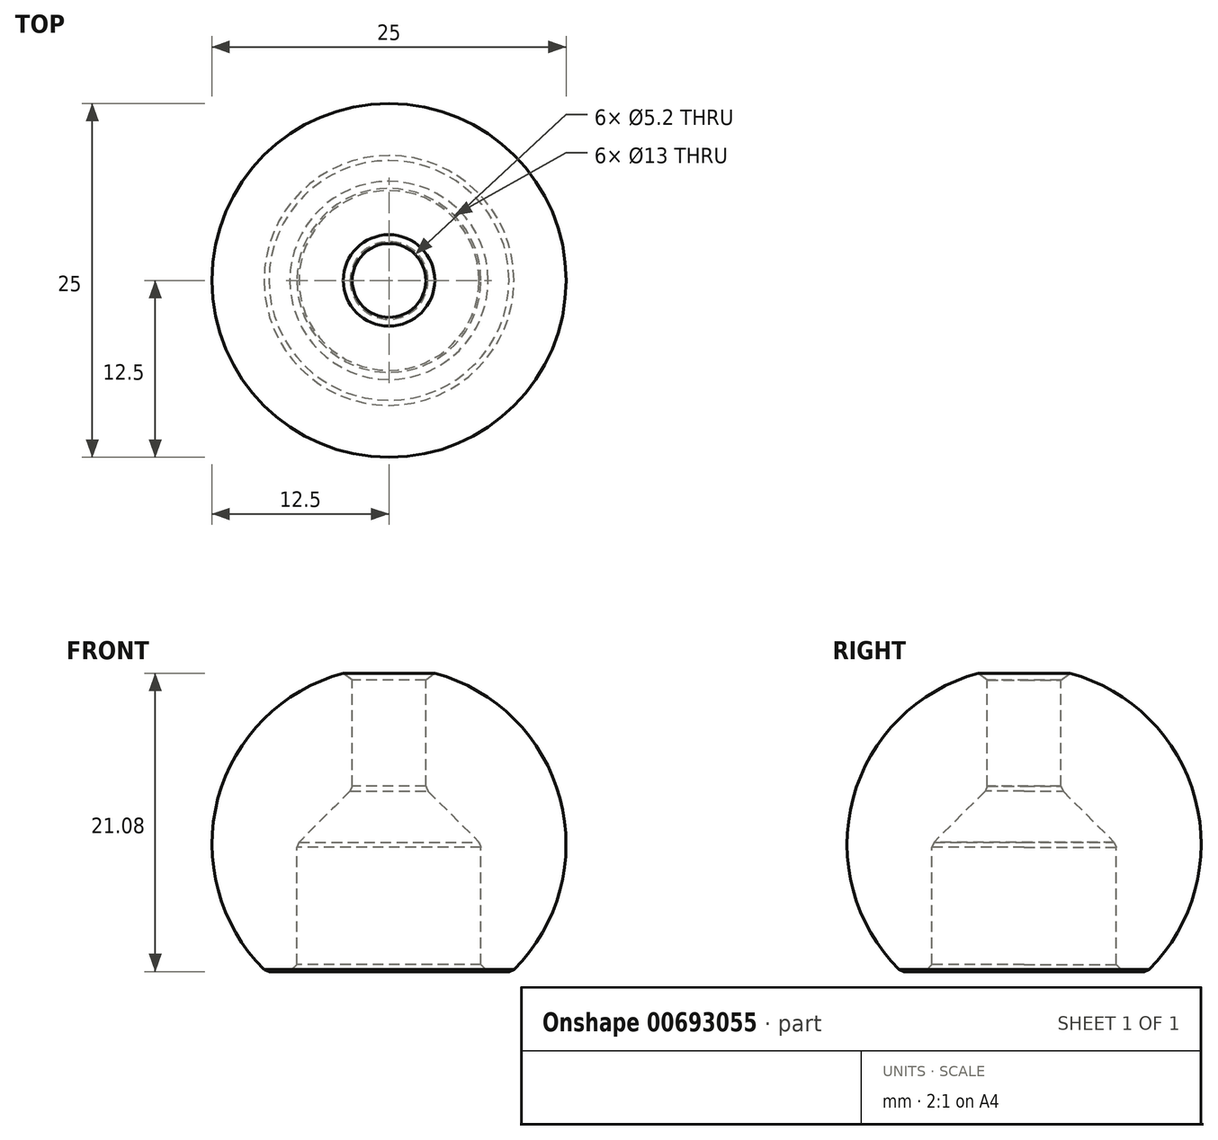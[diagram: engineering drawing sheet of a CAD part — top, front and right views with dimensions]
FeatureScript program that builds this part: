
annotation { "Feature Type Name" : "Feature", "Feature Type Description" : "" }
export const myFeature = defineFeature(function(context is Context, id is Id, definition is map)
    precondition{}
    {
        {
            var Q0;
            Q0=qCreatedBy(makeId("Front.planeOp"),FACE);
            var sketch = newSketch(context, id + "F0", { "sketchPlane" : qUnion([Q0])});
            skLineSegment(sketch, "E0", {"start": v(-8.67, -9) * mm, "end": v(-6.5, -9) * mm});
            skLineSegment(sketch, "E1", {"start": v(-2.6, 12.23) * mm, "end": v(-2.6, 3.9) * mm});
            skLineSegment(sketch, "E2", {"start": v(-2.6, 3.9) * mm, "end": v(-6.5, 0) * mm});
            skLineSegment(sketch, "E3", {"start": v(-6.5, 0) * mm, "end": v(-6.5, -9) * mm});
            skArc(sketch, "E4", {"start": v(-2.6, 12.23) * mm, "mid": v(-12.02, 3.44) * mm, "end": v(-8.67, -9) * mm});
            skArc(sketch, "E5", {"start": v(-8.67, -9) * mm, "mid": v(12.02, -3.44) * mm, "end": v(-2.6, 12.23) * mm, "construction": true});
            skLineSegment(sketch, "E6", {"start": v(0, 12.5) * mm, "end": v(0, -12.5) * mm, "construction": true});
            skSolve(sketch);
        }
        {
            var Q0;
            Q0 = qSketchRegion(id + "F0", true);
            var Q1;
            Q1=sQuery(id+"F0.wireOp",EDGE,"E6");
            revolve(context, id + "F1", {"entities" : qUnion([Q0]), "axis" : qUnion([Q1]), "revolveType" : RevolveType.FULL});
        }
        {
            var Q0;
            Q0=makeQuery(id+"F1.opRevolve","SWEPT_EDGE",EDGE,{"disambiguationData":[OSD([sQuery(id+"F0.wireOp",EDGE,"E1"),sQuery(id+"F0.wireOp",EDGE,"E4")])]});
            var Q1;
            Q1=makeQuery(id+"F1.opRevolve","SWEPT_EDGE",EDGE,{"disambiguationData":[OSD([sQuery(id+"F0.wireOp",EDGE,"E0"),sQuery(id+"F0.wireOp",EDGE,"E3")])]});
            var Q2;
            Q2=makeQuery(id+"F1.opRevolve","SWEPT_EDGE",EDGE,{"disambiguationData":[OSD([sQuery(id+"F0.wireOp",EDGE,"E2"),sQuery(id+"F0.wireOp",EDGE,"E3")])]});
            var Q3;
            Q3=makeQuery(id+"F1.opRevolve","SWEPT_EDGE",EDGE,{"disambiguationData":[OSD([sQuery(id+"F0.wireOp",EDGE,"E1"),sQuery(id+"F0.wireOp",EDGE,"E2")])]});
            var Q4;
            Q4=makeQuery(id+"F1.opRevolve","SWEPT_EDGE",EDGE,{"disambiguationData":[OSD([sQuery(id+"F0.wireOp",EDGE,"E0"),sQuery(id+"F0.wireOp",EDGE,"E4")])]});
            chamfer(context, id + "F2", {"entities" : qUnion([Q0, Q1, Q2, Q3, Q4]), "width" : 0.5 * mm, "tangentPropagation" : true});
        }
    });
